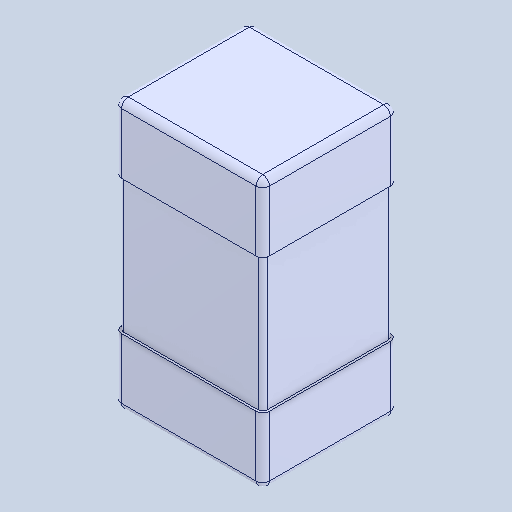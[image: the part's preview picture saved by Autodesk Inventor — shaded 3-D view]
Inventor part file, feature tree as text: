
AUTODESK INVENTOR PART (.ipt)
format: ipt  version: 2025 (Build 290162000, 162)  size: 128,000 bytes
history: native  units: mm
features: fillet x1, mirror x1, other x1
ambient origin geometry x8: Origin, YZ Plane, XZ Plane, XY Plane, X Axis, Y Axis, Z Axis, Center Point
bodies: Solid1 (feature_tree), Solid2 (feature_tree), Solid3 (feature_tree)
feature tree (3):
  fillet  "Fillet1"  [1 undecoded]
  mirror  "Mirror2"
  other  "Boss-Extrude2"
note: 1 required parameter value undecoded (feature->parameter linkage not recoverable at this tier; creation-order binding heuristic only, values carry confidence <= 0.55)
